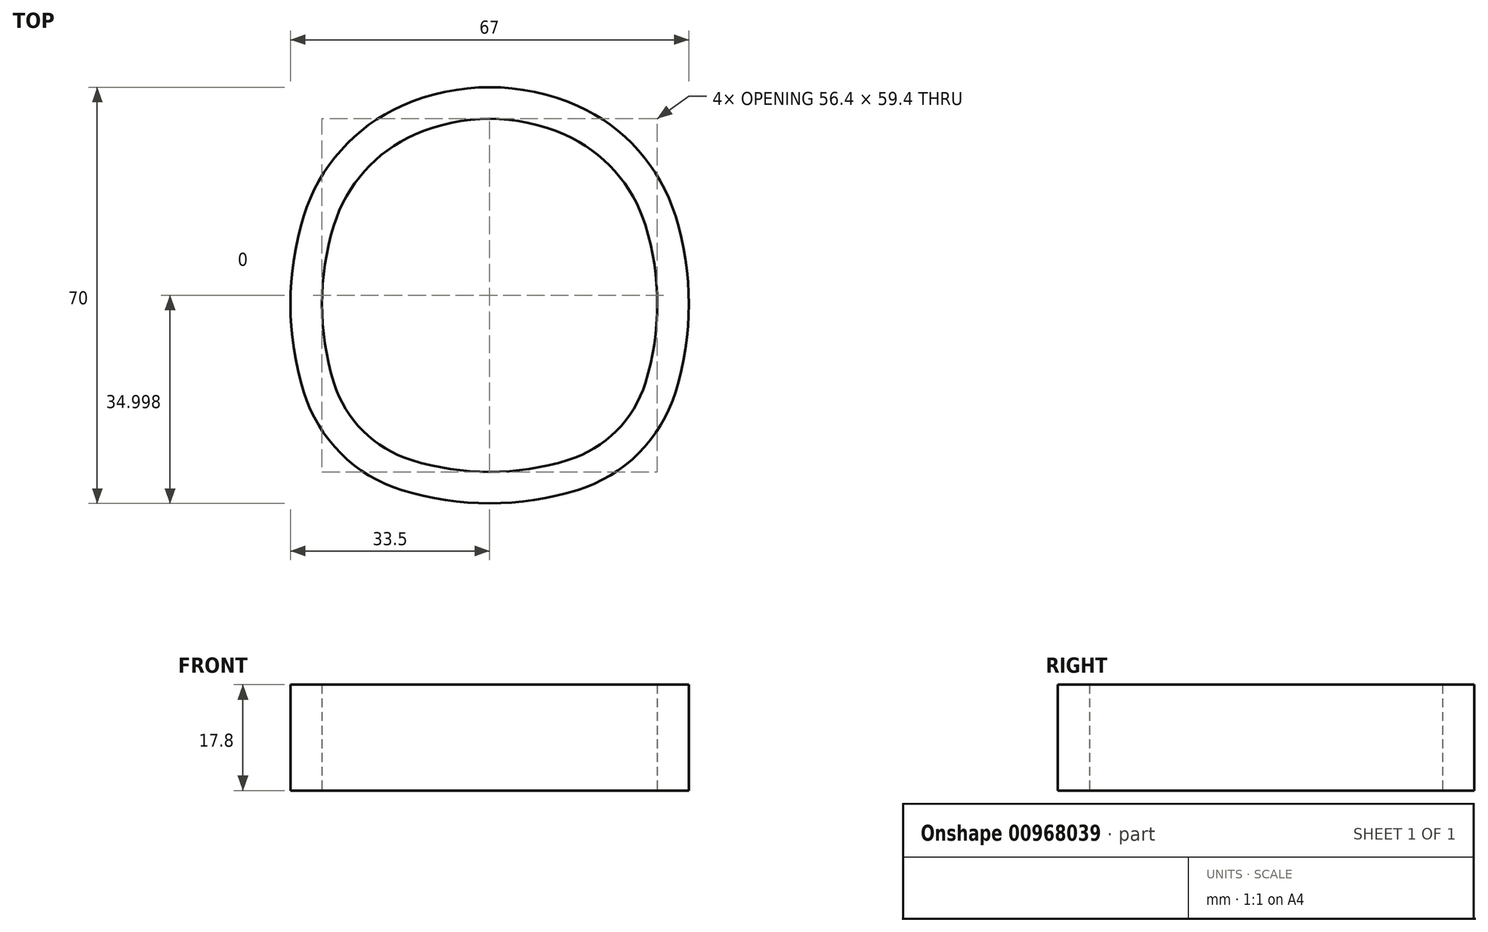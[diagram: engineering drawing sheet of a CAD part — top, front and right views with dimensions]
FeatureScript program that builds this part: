
annotation { "Feature Type Name" : "Feature", "Feature Type Description" : "" }
export const myFeature = defineFeature(function(context is Context, id is Id, definition is map)
    precondition{}
    {
        {
            var Q0;
            Q0=qCreatedBy(makeId("Top.planeOp"),FACE);
            var sketch = newSketch(context, id + "F0", { "sketchPlane" : qUnion([Q0])});
            skLineSegment(sketch, "E0", {"start": v(-31.25, 13.79) * mm, "end": v(-14.75, 32.33) * mm, "construction": true});
            skLineSegment(sketch, "E1", {"start": v(-14.75, 32.33) * mm, "end": v(14.75, 32.33) * mm, "construction": true});
            skLineSegment(sketch, "E2", {"start": v(14.75, 32.33) * mm, "end": v(31.25, 13.79) * mm, "construction": true});
            skLineSegment(sketch, "E3", {"start": v(31.25, 13.79) * mm, "end": v(31.25, -15.85) * mm, "construction": true});
            skLineSegment(sketch, "E4", {"start": v(31.25, -15.85) * mm, "end": v(14.75, -32.33) * mm, "construction": true});
            skLineSegment(sketch, "E5", {"start": v(14.75, -32.33) * mm, "end": v(-14.75, -32.33) * mm, "construction": true});
            skLineSegment(sketch, "E6", {"start": v(-14.75, -32.33) * mm, "end": v(-31.25, -15.85) * mm, "construction": true});
            skLineSegment(sketch, "E7", {"start": v(-31.25, -15.85) * mm, "end": v(-31.25, 13.79) * mm, "construction": true});
            skPoint(sketch, "E8", {"position": v(0, 0) * mm});
            skLineSegment(sketch, "E9", {"start": v(-31.25, -15.85) * mm, "end": v(31.25, -15.85) * mm, "construction": true});
            skLineSegment(sketch, "E10", {"start": v(-31.25, 13.79) * mm, "end": v(31.25, 13.79) * mm, "construction": true});
            skLineSegment(sketch, "E11", {"start": v(0, 32.33) * mm, "end": v(0, -32.33) * mm, "construction": true});
            skArc(sketch, "E12", {"start": v(14.75, 32.33) * mm, "mid": v(0, 35.45) * mm, "end": v(-14.75, 32.33) * mm});
            skArc(sketch, "E13", {"start": v(-14.75, 32.33) * mm, "mid": v(-25.01, 24.84) * mm, "end": v(-31.25, 13.79) * mm});
            skArc(sketch, "E14", {"start": v(14.75, 32.33) * mm, "mid": v(25.01, 24.84) * mm, "end": v(31.25, 13.79) * mm});
            skArc(sketch, "E15", {"start": v(-31.25, 13.79) * mm, "mid": v(-33.5, -1.03) * mm, "end": v(-31.25, -15.85) * mm});
            skArc(sketch, "E16", {"start": v(31.25, 13.79) * mm, "mid": v(33.5, -1.03) * mm, "end": v(31.25, -15.85) * mm});
            skArc(sketch, "E17", {"start": v(31.25, -15.85) * mm, "mid": v(25.04, -26.13) * mm, "end": v(14.75, -32.33) * mm});
            skArc(sketch, "E18", {"start": v(-31.25, -15.85) * mm, "mid": v(-25.04, -26.13) * mm, "end": v(-14.75, -32.33) * mm});
            skArc(sketch, "E19", {"start": v(-14.75, -32.33) * mm, "mid": v(0, -34.55) * mm, "end": v(14.75, -32.33) * mm});
            skLineSegment(sketch, "E20", {"start": v(0, 35.45) * mm, "end": v(0, -34.55) * mm, "construction": true});
            skLineSegment(sketch, "E21", {"start": v(-33.5, -1.03) * mm, "end": v(33.5, -1.03) * mm, "construction": true});
            skArc(sketch, "E22.0", {"start": v(12.6, 27.48) * mm, "mid": v(21.05, 21.32) * mm, "end": v(26.2, 12.22) * mm});
            skArc(sketch, "E22.1", {"start": v(12.6, 27.48) * mm, "mid": v(0, 30.15) * mm, "end": v(-12.6, 27.48) * mm});
            skArc(sketch, "E22.2", {"start": v(26.2, 12.22) * mm, "mid": v(28.2, -1.03) * mm, "end": v(26.2, -14.28) * mm});
            skArc(sketch, "E22.3", {"start": v(-12.6, 27.48) * mm, "mid": v(-21.05, 21.32) * mm, "end": v(-26.2, 12.22) * mm});
            skArc(sketch, "E22.4", {"start": v(26.2, -14.28) * mm, "mid": v(21.3, -22.38) * mm, "end": v(13.19, -27.26) * mm});
            skArc(sketch, "E22.5", {"start": v(-13.19, -27.26) * mm, "mid": v(0, -29.25) * mm, "end": v(13.19, -27.26) * mm});
            skArc(sketch, "E22.6", {"start": v(-26.2, -14.28) * mm, "mid": v(-21.3, -22.38) * mm, "end": v(-13.19, -27.26) * mm});
            skArc(sketch, "E22.7", {"start": v(-26.2, 12.22) * mm, "mid": v(-28.2, -1.03) * mm, "end": v(-26.2, -14.28) * mm});
            skSolve(sketch);
        }
        {
            var Q0;
            Q0 = qSketchRegion(id + "F0", true);
            extrude(context, id + "F1", {"entities" : qUnion([Q0]), "endBound" : BoundingType.SYMMETRIC, "depth" : 17.8 * mm, "offsetDistance" : 25 * mm});
        }
    });
